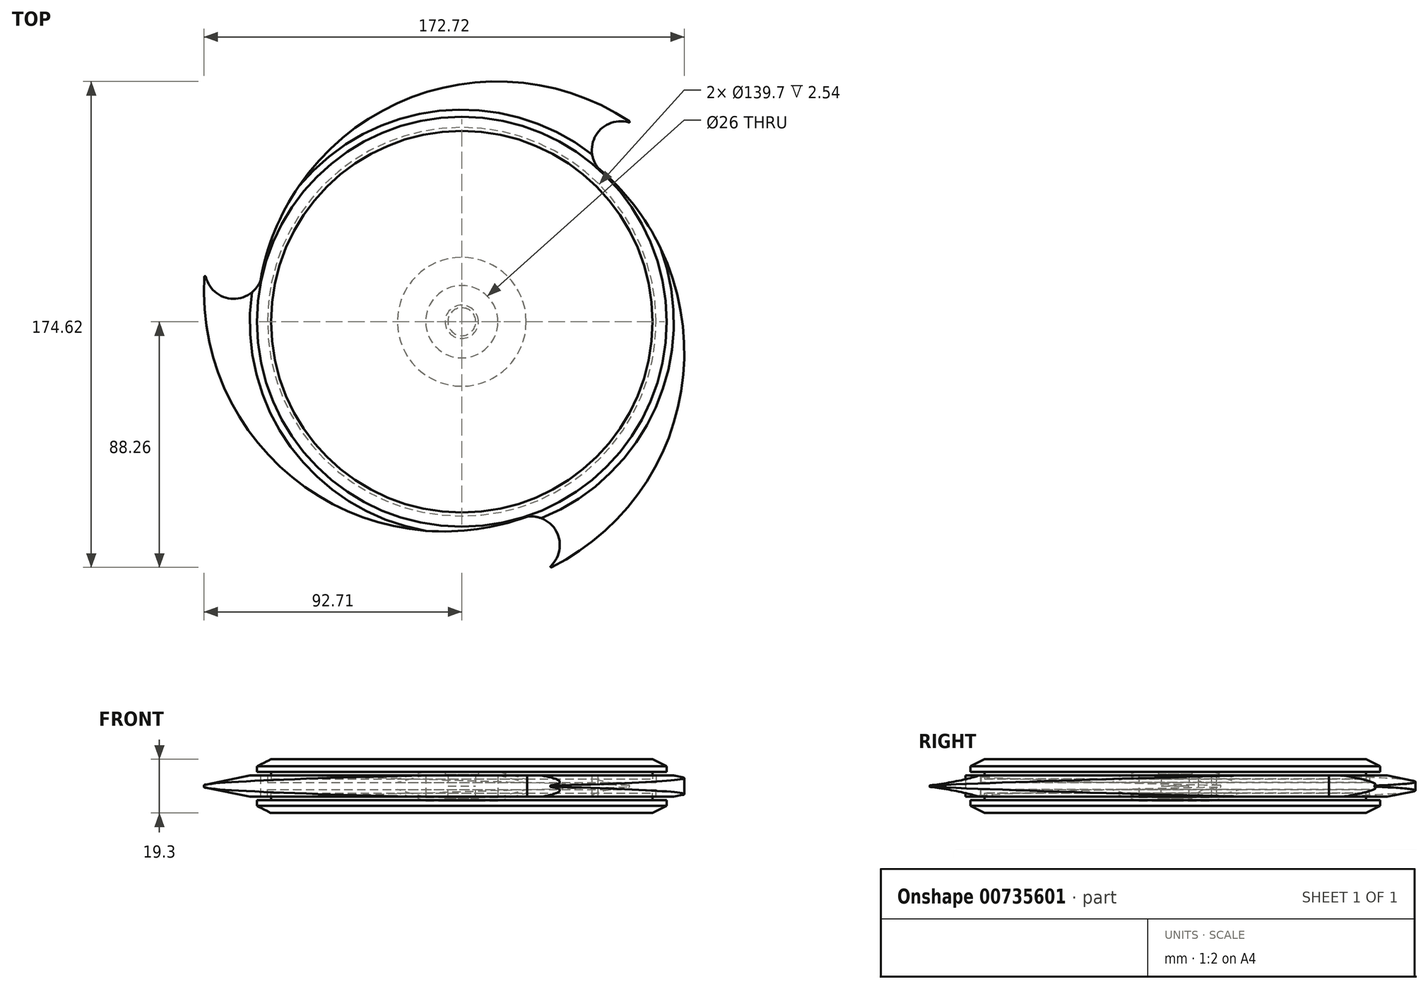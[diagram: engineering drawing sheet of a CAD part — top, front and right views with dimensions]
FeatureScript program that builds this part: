
annotation { "Feature Type Name" : "Feature", "Feature Type Description" : "" }
export const myFeature = defineFeature(function(context is Context, id is Id, definition is map)
    precondition{}
    {
        {
            var Q0;
            Q0=qCreatedBy(makeId("Front.planeOp"),FACE);
            var sketch = newSketch(context, id + "F0", { "sketchPlane" : qUnion([Q0])});
            skLineSegment(sketch, "E0", {"start": v(0, 0) * mm, "end": v(-13, 0) * mm});
            skLineSegment(sketch, "E1", {"start": v(-13, 0) * mm, "end": v(-13, 4) * mm});
            skPoint(sketch, "E2", {"position": v(-23.16, 0) * mm});
            skPoint(sketch, "E3", {"position": v(-23.16, 1.27) * mm});
            skLineSegment(sketch, "E4", {"start": v(-13, 4) * mm, "end": v(-23.16, 1.27) * mm});
            skPoint(sketch, "E5", {"position": v(-73.66, 0) * mm});
            skPoint(sketch, "E6", {"position": v(-73.66, 1.27) * mm});
            skLineSegment(sketch, "E7", {"start": v(-69.85, 1.27) * mm, "end": v(-23.16, 1.27) * mm});
            skLineSegment(sketch, "E8", {"start": v(-73.66, 1.27) * mm, "end": v(-73.66, 0) * mm});
            skLineSegment(sketch, "E9", {"start": v(-73.66, 0) * mm, "end": v(-13, 0) * mm});
            skLineSegment(sketch, "E10", {"start": v(0, 0) * mm, "end": v(0, -11.3) * mm});
            skLineSegment(sketch, "E11", {"start": v(0, -11.3) * mm, "end": v(0, 11.88) * mm});
            skLineSegment(sketch, "E12", {"start": v(-73.66, 1.27) * mm, "end": v(-73.66, 3.81) * mm});
            skLineSegment(sketch, "E13", {"start": v(-73.66, 3.81) * mm, "end": v(-69.85, 3.81) * mm});
            skLineSegment(sketch, "E14", {"start": v(-69.85, 3.81) * mm, "end": v(-69.85, 1.27) * mm});
            skSolve(sketch);
        }
        {
            var Q0;
            Q0=makeQuery(id+"F0.imprint","IMPRINT",FACE,{"disambiguationData":[TD([[makeQuery(id+"F0.imprint","IMPRINT",EDGE,{"derivedFrom":sQuery(id+"F0.wireOp",EDGE,"E1")}),1.0]])]});
            var Q1;
            Q1=sQuery(id+"F0.wireOp",EDGE,"E11");
            revolve(context, id + "F1", {"surfaceOperationType" : NewSurfaceOperationType.NEW, "entities" : qUnion([Q0]), "axis" : qUnion([Q1]), "revolveType" : RevolveType.FULL});
        }
        {
            var Q0;
            Q0=makeQuery(id+"F1.opRevolve","SWEPT_BODY",BODY,{"disambiguationData":[OSD([sQuery(id+"F0.wireOp",EDGE,"E1"),sQuery(id+"F0.wireOp",EDGE,"E4"),sQuery(id+"F0.wireOp",EDGE,"E7"),sQuery(id+"F0.wireOp",EDGE,"E8"),sQuery(id+"F0.wireOp",EDGE,"E9"),sQuery(id+"F0.wireOp",EDGE,"E12"),sQuery(id+"F0.wireOp",EDGE,"E13"),sQuery(id+"F0.wireOp",EDGE,"E14")])]});
            var Q1;
            Q1=makeQuery(id+"F1.opRevolve","SWEPT_FACE",FACE,{"disambiguationData":[OSD([sQuery(id+"F0.wireOp",EDGE,"E9")])]});
            mirror(context, id + "F2", {"operationType" : NewBodyOperationType.ADD, "entities" : qUnion([Q0]), "mirrorPlane" : qUnion([Q1])});
        }
        {
            var Q0;
            Q0=qCreatedBy(makeId("Top.planeOp"),FACE);
            var sketch = newSketch(context, id + "F3", { "sketchPlane" : qUnion([Q0])});
            skArc(sketch, "E15", {"start": v(64.15, 69.36) * mm, "mid": v(-26.12, 77.14) * mm, "end": v(-73.66, 0) * mm});
            skCircle(sketch, "E16", {"center": v(0, 0) * mm, "radius": 73.66 * mm});
            skLineSegment(sketch, "E17", {"start": v(50.02, 54.08) * mm, "end": v(50.06, 54.13) * mm});
            skArc(sketch, "E18", {"start": v(64.1, 69.3) * mm, "mid": v(49.5, 68.74) * mm, "end": v(50.06, 54.13) * mm});
            skLineSegment(sketch, "E19.trimOffspring", {"start": v(64.1, 69.3) * mm, "end": v(64.15, 69.36) * mm});
            skSolve(sketch);
        }
        {
            var Q0;
            {var subQ5=sQuery(id+"F3.wireOp",EDGE,"E17");Q0=makeQuery(id+"F3.imprint","IMPRINT",FACE,{"disambiguationData":[TD([[makeQuery(id+"F3.imprint","IMPRINT",EDGE,{"derivedFrom":subQ5}),1.0]])]});}
            extrude(context, id + "F4", {"entities" : qUnion([Q0]), "endBound" : BoundingType.SYMMETRIC, "depth" : 7.62 * mm, "offsetDistance" : 25.4 * mm});
        }
        {
            var Q0;
            Q0=makeQuery(id+"F4.opExtrude","SWEPT_BODY",BODY,{"disambiguationData":[OSD([sQuery(id+"F3.wireOp",EDGE,"E15"),sQuery(id+"F3.wireOp",EDGE,"E16"),sQuery(id+"F3.wireOp",EDGE,"E17"),sQuery(id+"F3.wireOp",EDGE,"E18")])]});
            var Q1;
            Q1=sQuery(id+"F0.wireOp",EDGE,"E11");
            circularPattern(context, id + "F5", {"entities" : qUnion([Q0]), "axis" : qUnion([Q1]), "angle" : 360 * degree, "instanceCount" : 3, "equalSpace" : true});
        }
        {
            var Q0;
            Q0=makeQuery(id+"F5.opPattern","COPY",EDGE,{"derivedFrom":makeQuery(id+"F4.opExtrude","SWEPT_EDGE",EDGE,{"disambiguationData":[OSD([sQuery(id+"F3.wireOp",EDGE,"E15"),sQuery(id+"F3.wireOp",EDGE,"E18")])]}),"instanceName":"2"});
            var Q1;
            Q1=makeQuery(id+"F4.opExtrude","SWEPT_EDGE",EDGE,{"disambiguationData":[OSD([sQuery(id+"F3.wireOp",EDGE,"E15"),sQuery(id+"F3.wireOp",EDGE,"E18")])]});
            var Q2;
            Q2=makeQuery(id+"F5.opPattern","COPY",EDGE,{"derivedFrom":makeQuery(id+"F4.opExtrude","SWEPT_EDGE",EDGE,{"disambiguationData":[OSD([sQuery(id+"F3.wireOp",EDGE,"E15"),sQuery(id+"F3.wireOp",EDGE,"E18")])]}),"instanceName":"1"});
            fillet(context, id + "F6", {"entities" : qUnion([Q0, Q1, Q2]), "radius" : 0.25 * mm, "tangentPropagation" : true, "allowEdgeOverflow" : false});
        }
        {
            var Q0;
            Q0=makeQuery(id+"F4.opExtrude","SWEPT_BODY",BODY,{"disambiguationData":[OSD([sQuery(id+"F3.wireOp",EDGE,"E15"),sQuery(id+"F3.wireOp",EDGE,"E16"),sQuery(id+"F3.wireOp",EDGE,"E17"),sQuery(id+"F3.wireOp",EDGE,"E18")])]});
            var Q1;
            Q1=makeQuery(id+"F5.opPattern","COPY",BODY,{"derivedFrom":makeQuery(id+"F4.opExtrude","SWEPT_BODY",BODY,{"disambiguationData":[OSD([sQuery(id+"F3.wireOp",EDGE,"E15"),sQuery(id+"F3.wireOp",EDGE,"E16"),sQuery(id+"F3.wireOp",EDGE,"E17"),sQuery(id+"F3.wireOp",EDGE,"E18")])]}),"instanceName":"1"});
            var Q2;
            Q2=makeQuery(id+"F5.opPattern","COPY",BODY,{"derivedFrom":makeQuery(id+"F4.opExtrude","SWEPT_BODY",BODY,{"disambiguationData":[OSD([sQuery(id+"F3.wireOp",EDGE,"E15"),sQuery(id+"F3.wireOp",EDGE,"E16"),sQuery(id+"F3.wireOp",EDGE,"E17"),sQuery(id+"F3.wireOp",EDGE,"E18")])]}),"instanceName":"2"});
            var Q3;
            Q3=makeQuery(id+"F1.opRevolve","SWEPT_BODY",BODY,{"disambiguationData":[OSD([sQuery(id+"F0.wireOp",EDGE,"E1"),sQuery(id+"F0.wireOp",EDGE,"E4"),sQuery(id+"F0.wireOp",EDGE,"E7"),sQuery(id+"F0.wireOp",EDGE,"E8"),sQuery(id+"F0.wireOp",EDGE,"E9"),sQuery(id+"F0.wireOp",EDGE,"E12"),sQuery(id+"F0.wireOp",EDGE,"E13"),sQuery(id+"F0.wireOp",EDGE,"E14")])]});
            booleanBodies(context, id + "F7", {"operationType" : BooleanOperationType.UNION, "tools" : qUnion([Q0, Q1, Q2, Q3])});
        }
        {
            var Q0;
            Q0=qCreatedBy(makeId("Front.planeOp"),FACE);
            var sketch = newSketch(context, id + "F8", { "sketchPlane" : qUnion([Q0])});
            skPoint(sketch, "E20", {"position": v(-94.95, 0) * mm});
            skLineSegment(sketch, "E21", {"start": v(-76.22, 3.81) * mm, "end": v(-94.95, 0) * mm});
            skLineSegment(sketch, "E22", {"start": v(-94.95, 0) * mm, "end": v(-76.22, -3.81) * mm});
            skLineSegment(sketch, "E23", {"start": v(-94.95, 0) * mm, "end": v(-94.95, -3.81) * mm});
            skLineSegment(sketch, "E24", {"start": v(-94.95, -3.81) * mm, "end": v(-94.95, 3.8) * mm});
            skLineSegment(sketch, "E25", {"start": v(-76.22, 3.81) * mm, "end": v(-94.95, 3.8) * mm});
            skLineSegment(sketch, "E26", {"start": v(-76.22, -3.81) * mm, "end": v(-94.95, -3.81) * mm});
            skSolve(sketch);
        }
        {
            var Q0;
            {var subQ0=sQuery(id+"F8.wireOp",EDGE,"E21");Q0=makeQuery(id+"F8.imprint","IMPRINT",FACE,{"disambiguationData":[TD([[makeQuery(id+"F8.imprint","IMPRINT",EDGE,{"derivedFrom":subQ0}),-1.0]])]});}
            var Q1;
            {var subQ0=sQuery(id+"F8.wireOp",EDGE,"E22");Q1=makeQuery(id+"F8.imprint","IMPRINT",FACE,{"disambiguationData":[TD([[makeQuery(id+"F8.imprint","IMPRINT",EDGE,{"derivedFrom":subQ0}),-1.0]])]});}
            var Q2;
            Q2=sQuery(id+"F0.wireOp",EDGE,"E11");
            revolve(context, id + "F9", {"operationType" : NewBodyOperationType.REMOVE, "surfaceOperationType" : NewSurfaceOperationType.NEW, "entities" : qUnion([Q0, Q1]), "axis" : qUnion([Q2]), "revolveType" : RevolveType.FULL, "oppositeDirection" : true});
        }
        {
            var Q0;
            Q0=qCreatedBy(makeId("Front.planeOp"),FACE);
            var sketch = newSketch(context, id + "F10", { "sketchPlane" : qUnion([Q0])});
            skPoint(sketch, "E27", {"position": v(-73.66, 3.81) * mm});
            skPoint(sketch, "E28", {"position": v(-73.66, 5.08) * mm});
            skPoint(sketch, "E29", {"position": v(-68.58, 2.54) * mm});
            skPoint(sketch, "E30", {"position": v(-68.58, 5.08) * mm});
            skLineSegment(sketch, "E31", {"start": v(-73.66, 5.08) * mm, "end": v(-68.58, 5.08) * mm});
            skLineSegment(sketch, "E32", {"start": v(-68.58, 5.08) * mm, "end": v(-68.58, 2.54) * mm});
            skPoint(sketch, "E33", {"position": v(-23.16, 1.27) * mm});
            skPoint(sketch, "E34", {"position": v(-23.16, 2.54) * mm});
            skLineSegment(sketch, "E35", {"start": v(-68.58, 2.54) * mm, "end": v(-23.16, 2.54) * mm});
            skLineSegment(sketch, "E36", {"start": v(-23.16, 2.54) * mm, "end": v(-13, 5.27) * mm});
            skPoint(sketch, "E37", {"position": v(-13, 4) * mm});
            skLineSegment(sketch, "E38", {"start": v(-13, 5.27) * mm, "end": v(-6, 5.27) * mm});
            skLineSegment(sketch, "E39", {"start": v(-5, 4.27) * mm, "end": v(-5, 0) * mm});
            skLineSegment(sketch, "E40", {"start": v(-5, 0) * mm, "end": v(0, 0) * mm});
            skLineSegment(sketch, "E41", {"start": v(-73.66, 5.08) * mm, "end": v(-73.66, 7.11) * mm});
            skPoint(sketch, "E42", {"position": v(-68.58, 9.65) * mm});
            skLineSegment(sketch, "E43", {"start": v(-73.66, 7.11) * mm, "end": v(-68.58, 9.65) * mm});
            skLineSegment(sketch, "E44", {"start": v(-68.58, 9.65) * mm, "end": v(0, 9.65) * mm});
            skLineSegment(sketch, "E45", {"start": v(0, 9.65) * mm, "end": v(0, 0) * mm});
            skPoint(sketch, "E46", {"position": v(-6, 5.27) * mm});
            skPoint(sketch, "E47", {"position": v(-5, 4.27) * mm});
            skLineSegment(sketch, "E48", {"start": v(-6, 5.27) * mm, "end": v(-6, 4.27) * mm});
            skLineSegment(sketch, "E49", {"start": v(-5, 4.27) * mm, "end": v(-6, 4.27) * mm});
            skPoint(sketch, "E50.orphan", {"position": v(-5, 5.27) * mm});
            skSolve(sketch);
        }
        {
            var Q0;
            Q0=makeQuery(id+"F10.imprint","IMPRINT",FACE,{"disambiguationData":[TD([[makeQuery(id+"F10.imprint","IMPRINT",EDGE,{"derivedFrom":sQuery(id+"F10.wireOp",EDGE,"E31")}),1.0]])]});
            var Q1;
            Q1=sQuery(id+"F0.wireOp",EDGE,"E11");
            revolve(context, id + "F11", {"surfaceOperationType" : NewSurfaceOperationType.NEW, "entities" : qUnion([Q0]), "axis" : qUnion([Q1]), "revolveType" : RevolveType.FULL});
        }
        {
            var Q0;
            Q0=makeQuery(id+"F11.opRevolve","SWEPT_BODY",BODY,{"disambiguationData":[OSD([sQuery(id+"F10.wireOp",EDGE,"E31"),sQuery(id+"F10.wireOp",EDGE,"E32"),sQuery(id+"F10.wireOp",EDGE,"E35"),sQuery(id+"F10.wireOp",EDGE,"E36"),sQuery(id+"F10.wireOp",EDGE,"E38"),sQuery(id+"F10.wireOp",EDGE,"E39"),sQuery(id+"F10.wireOp",EDGE,"E40"),sQuery(id+"F10.wireOp",EDGE,"E41"),sQuery(id+"F10.wireOp",EDGE,"E43"),sQuery(id+"F10.wireOp",EDGE,"E44"),sQuery(id+"F10.wireOp",EDGE,"E45")])]});
            var Q1;
            Q1=makeQuery(id+"F11.opRevolve","SWEPT_FACE",FACE,{"disambiguationData":[OSD([sQuery(id+"F10.wireOp",EDGE,"E40")])]});
            mirror(context, id + "F12", {"entities" : qUnion([Q0]), "mirrorPlane" : qUnion([Q1])});
        }
    });
